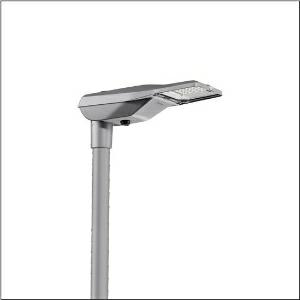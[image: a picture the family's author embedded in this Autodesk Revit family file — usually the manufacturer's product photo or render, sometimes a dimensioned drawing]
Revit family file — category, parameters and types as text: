
# Revit family: streetlight_sl_21_iq_micro___st1_0ab_5xe1m31u08cb_f63b
name_source: partatom
category: Lighting Fixtures
units: mm (PartAtom-declared; Revit-internal decimal feet)

## family parameters
Cut with Voids When Loaded = No
Host = Face
Light Source = No
Part Type = Normal
Room Calculation Point = No
Round Connector Dimension = Use Diameter
Shared = No

## types (1)
- --- (1 x LED, 2530 lm, 19.1 W, 3000K)
    Apparent Load = 19 VA
    CIE Flux Codes = 38 73 97 100 100
    Color Rendering = 70
    Color Temperature = 3000K
    Default Elevation = 1800 mm
    Description = Streetlight SL 21 iQ micro, mast luminaire, primary light control with lens, of PMMA, primary optical cover: cover, of toughened safety glass, transparent, light distribution: ST1.0aB, light emission: direct distribution, primary light characteristic: asymmetric, installation type: post-top, side-entry, LED, High Power LED, rated luminous flux: 2.530lm, luminous efficacy: 133lm/W, light colour: 730, colour temperature: 3000K, control gear: iQ-Street Remote, D4i with power reduction, control: pre-setting: logarithmic dimming characteristic, Street-Remote, Auto-Match, Temp-Guard, Lumen-Switch, Night-Set, Smart-Wire, Light-Fading, Desk-Remote (wireless, voltage-free reading and setting of iQ features in the workshop via application-optimized NFC function/RFID function), optimised constant luminous flux control (CLO 2.0), mains connection: 220..240V, AC, 50/60Hz, start of lifetime: 19W, end of service life: 20W, reduction: 9W, luminaire housing, of diecast aluminium, powder-coated, Siteco® metallic grey (DB 702S), corrosivity category C5 mid according to DIN EN ISO 12944, please order mast flange separately, inclination adjustable: 0°, 5°, 10°, 15°, sealing non-destructively replaceable, multi-level sealing system, length: 528mm, width: 235mm, height: 110mm, mast flange for spigot size: 42mm (side-entry): 5XC10008XM4, 60/48mm (side-entry/post-top): 5XC10108XM2, 76/60mm (side-entry/post-top): 5XC10108XM1, mounting height: 4..8m, Smart Interface below, protection rating (complete): IP66, insulation class (complete): insulation class II (safety insulation), certification: CE, ENEC, ENEC+, VDE, impact resistance: IK10, permissible operating ambient temperature for outdoor applications: -40..+50°C, standard-compliant lighting for roads and squares, packaging unit: 1 piece

Light Distribution: ST1.0aB
    Height = 110 mm
    Lamp = 1 x LED
    Lamp Light Flux = 2530 lm
    Lamp Power = 19.1 W
    Lamp count = 1
    Length = 528 mm
    Luminous efficacy = 132 lm/W
    Manufacturer = Siteco
    ModVariant = No
    Model = 5XE1M31U08CB
    Number of Poles = 1
    OnlyDefault = Yes
    Power Factor = 1
    Product Name = Streetlight SL 21 iQ micro | ST1.0aB
    Product group = mast luminaire | pylon top
    ProductGroupID = 6100
    Protection Class = Protection class II
    Protection Degree = IP 66
    RLX_Detail_Level = 1
    RLX_Emergency_Light_Flux = 0 lm
    RLX_Emergency_Type = 0
    RLX_Emergency_Type_DB = No
    RlxData = <blob elided: 99313 chars, md5=782fe253>
    Socket = socket
    Standby Power = 0 W
    System Light Flux = 2530 lm
    System Power = 19 W
    Type Comments = factory setting: luminous flux: 100 % | dim-lin: 254 | 387 mA
    Type Image = l_1277290.jpg
    URL = http://relux.com
    VarID = @adj_112824
    Voltage = 0 V
    Weight = 0.00 kg
    Width = 235 mm

## geometry (parser evidence)
native form markers: Blend x4, Sweep x10
no freeform markers — native parametric forms only
